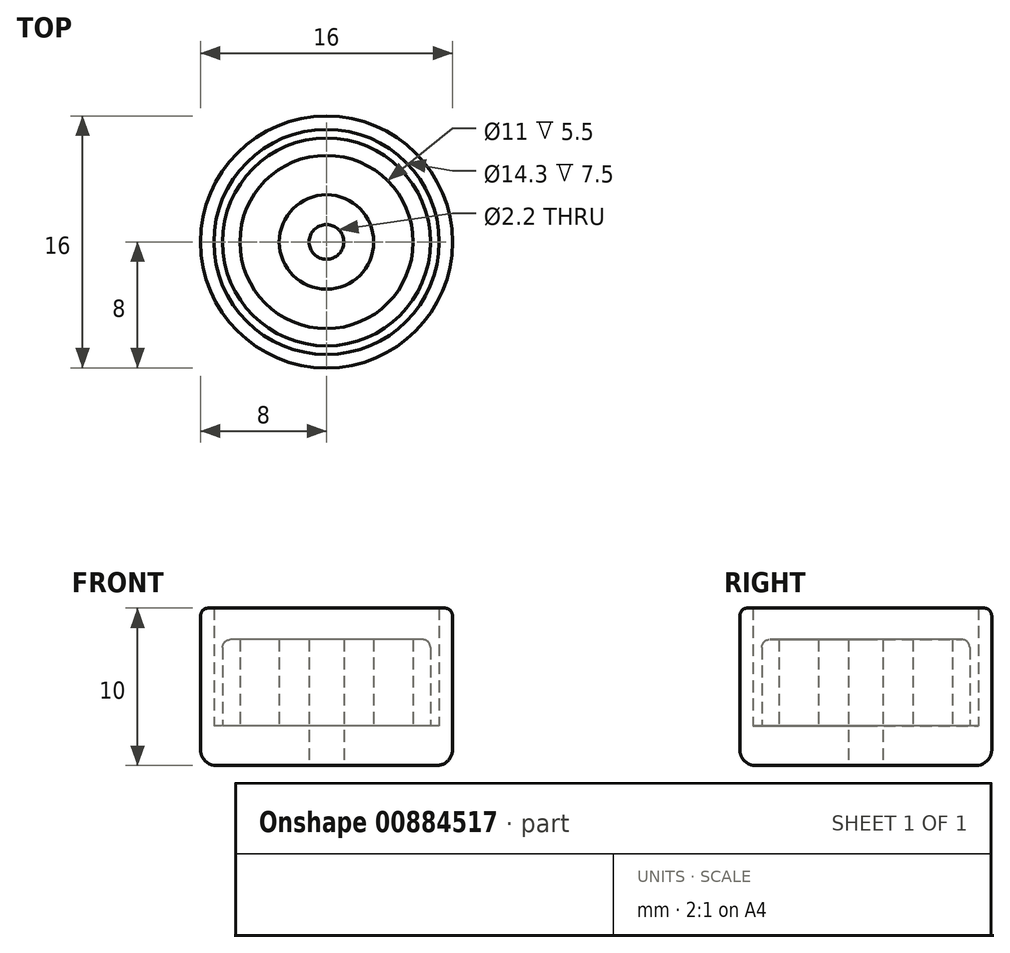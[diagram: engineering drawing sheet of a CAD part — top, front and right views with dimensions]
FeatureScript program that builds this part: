
annotation { "Feature Type Name" : "Feature", "Feature Type Description" : "" }
export const myFeature = defineFeature(function(context is Context, id is Id, definition is map)
    precondition{}
    {
        {
            var Q0;
            Q0=qCreatedBy(makeId("Top.planeOp"),FACE);
            var sketch = newSketch(context, id + "F0", { "sketchPlane" : qUnion([Q0])});
            skCircle(sketch, "E0", {"center": v(0, 0) * mm, "radius": 6.6 * mm});
            skCircle(sketch, "E1", {"center": v(0, 0) * mm, "radius": 7.15 * mm});
            skCircle(sketch, "E2", {"center": v(0, 0) * mm, "radius": 5.5 * mm});
            skCircle(sketch, "E3", {"center": v(0, 0) * mm, "radius": 8 * mm});
            skCircle(sketch, "E4", {"center": v(0, 0) * mm, "radius": 1.1 * mm});
            skCircle(sketch, "E5", {"center": v(0, 0) * mm, "radius": 3 * mm});
            skSolve(sketch);
        }
        {
            var Q0;
            Q0=makeQuery(id+"F0.imprint","IMPRINT",FACE,{"disambiguationData":[TD([[makeQuery(id+"F0.imprint","IMPRINT",EDGE,{"derivedFrom":sQuery(id+"F0.wireOp",EDGE,"E0")}),1.0]])]});
            extrude(context, id + "F1", {"entities" : qUnion([Q0]), "depth" : 6 * mm, "offsetDistance" : 25 * mm});
        }
        {
            var Q0;
            Q0=makeQuery(id+"F0.imprint","IMPRINT",FACE,{"disambiguationData":[TD([[makeQuery(id+"F0.imprint","IMPRINT",EDGE,{"derivedFrom":sQuery(id+"F0.wireOp",EDGE,"E0")}),-1.0]])]});
            var Q1;
            Q1=makeQuery(id+"F0.imprint","IMPRINT",FACE,{"disambiguationData":[TD([[makeQuery(id+"F0.imprint","IMPRINT",EDGE,{"derivedFrom":sQuery(id+"F0.wireOp",EDGE,"E2")}),1.0]])]});
            extrude(context, id + "F2", {"entities" : qUnion([Q0, Q1]), "operationType" : NewBodyOperationType.ADD, "depth" : .5 * mm, "offsetDistance" : 25 * mm});
        }
        {
            var Q0;
            Q0=makeQuery(id+"F0.imprint","IMPRINT",FACE,{"disambiguationData":[TD([[makeQuery(id+"F0.imprint","IMPRINT",EDGE,{"derivedFrom":sQuery(id+"F0.wireOp",EDGE,"E1")}),-1.0]])]});
            extrude(context, id + "F3", {"entities" : qUnion([Q0]), "operationType" : NewBodyOperationType.ADD, "depth" : 8 * mm, "offsetDistance" : 25 * mm});
        }
        {
            var Q0;
            Q0=makeQuery(id+"F0.imprint","IMPRINT",FACE,{"disambiguationData":[TD([[makeQuery(id+"F0.imprint","IMPRINT",EDGE,{"derivedFrom":sQuery(id+"F0.wireOp",EDGE,"E4")}),-1.0]])]});
            extrude(context, id + "F4", {"entities" : qUnion([Q0]), "operationType" : NewBodyOperationType.ADD, "depth" : 6 * mm, "offsetDistance" : 25 * mm});
        }
        {
            var Q0;
            Q0=makeQuery(id+"F1.opExtrude","CAP_EDGE",EDGE,{"disambiguationData":[OSD([sQuery(id+"F0.wireOp",EDGE,"E0")])],"isStart":false});
            var Q1;
            Q1=makeQuery(id+"F3.opExtrude","CAP_EDGE",EDGE,{"disambiguationData":[OSD([sQuery(id+"F0.wireOp",EDGE,"E3")])],"isStart":false});
            fillet(context, id + "F5", {"entities" : qUnion([Q0, Q1]), "tangentPropagation" : true, "radius" : 0.5 * mm, "defaultsChanged" : false, "vertexSettings" : [], "allowEdgeOverflow" : false});
        }
        {
            var Q0;
            {var subQ0=sQuery(id+"F0.wireOp",EDGE,"E5");var subQ1=sQuery(id+"F0.wireOp",EDGE,"E1");var subQ2=sQuery(id+"F0.wireOp",EDGE,"E2");var subQ3=sQuery(id+"F0.wireOp",EDGE,"E0");Q0=makeQuery(id+"F4.boolean.opBoolean","MERGE",FACE,{"derivedFrom":[makeQuery(id+"F3.boolean.opBoolean","MERGE",FACE,{"derivedFrom":[makeQuery(id+"F2.boolean.opBoolean","MERGE",FACE,{"derivedFrom":[makeQuery(id+"F1.opExtrude","CAP_FACE",FACE,{"disambiguationData":[OSD([subQ3,subQ2])],"isStart":true}),makeQuery(id+"F2.opExtrude","CAP_FACE",FACE,{"disambiguationData":[OSD([subQ3,subQ1])],"isStart":true}),makeQuery(id+"F2.opExtrude","CAP_FACE",FACE,{"disambiguationData":[OSD([subQ2,subQ0])],"isStart":true})]}),makeQuery(id+"F3.opExtrude","CAP_FACE",FACE,{"disambiguationData":[OSD([subQ1,sQuery(id+"F0.wireOp",EDGE,"E3")])],"isStart":true})]}),makeQuery(id+"F4.opExtrude","CAP_FACE",FACE,{"disambiguationData":[OSD([sQuery(id+"F0.wireOp",EDGE,"E4"),subQ0])],"isStart":true})]});}
            extrude(context, id + "F6", {"entities" : qUnion([Q0]), "operationType" : NewBodyOperationType.ADD, "depth" : 2 * mm, "offsetDistance" : 25 * mm});
        }
        {
            var Q0;
            Q0=makeQuery(id+"F6.opExtrude","CAP_EDGE",EDGE,{"disambiguationData":[OSD([sQuery(id+"F0.wireOp",EDGE,"E3")])],"isStart":false});
            fillet(context, id + "F7", {"entities" : qUnion([Q0]), "tangentPropagation" : true, "radius" : 1 * mm, "defaultsChanged" : false, "vertexSettings" : [], "allowEdgeOverflow" : false});
        }
    });
